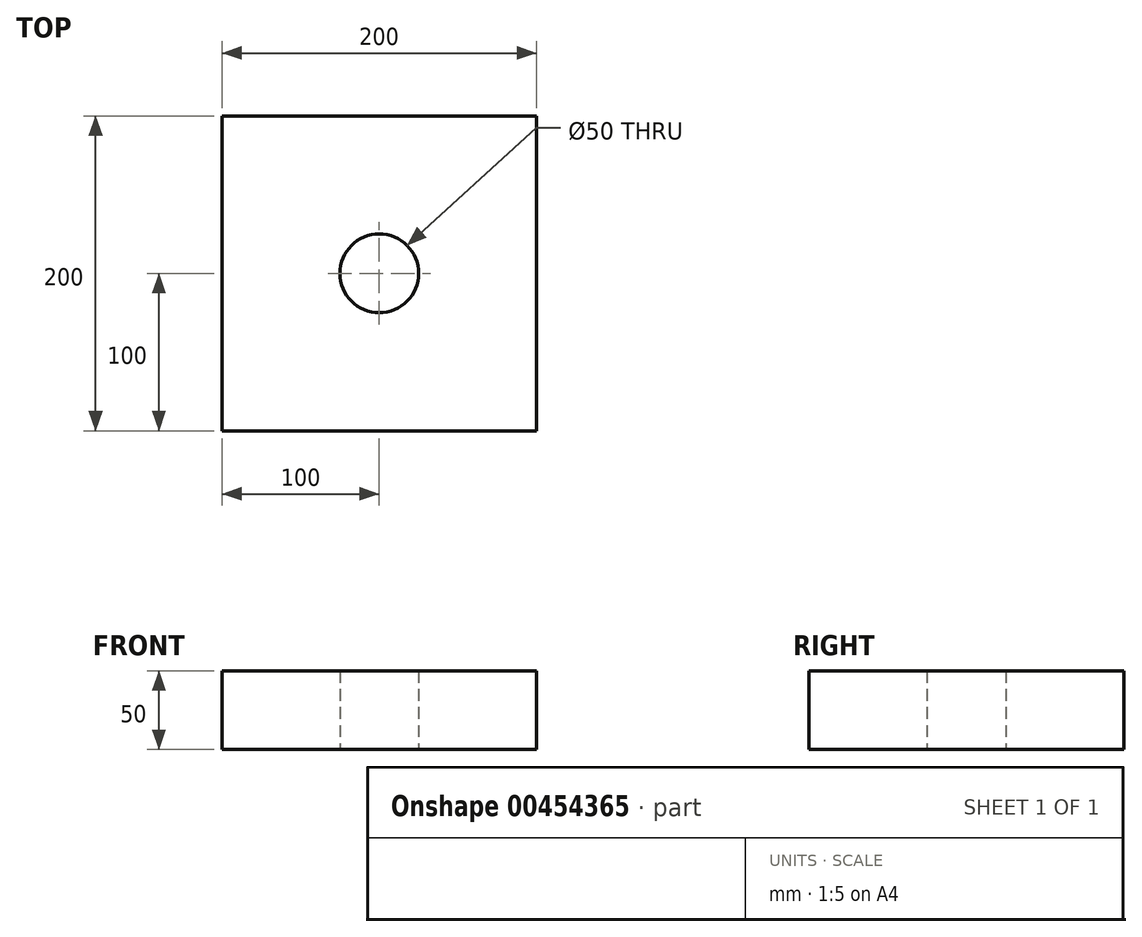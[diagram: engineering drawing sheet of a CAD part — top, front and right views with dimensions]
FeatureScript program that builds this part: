
annotation { "Feature Type Name" : "Feature", "Feature Type Description" : "" }
export const myFeature = defineFeature(function(context is Context, id is Id, definition is map)
    precondition{}
    {
        {
            var Q0;
            Q0=qCreatedBy(makeId("Top.planeOp"),FACE);
            var sketch = newSketch(context, id + "F0", { "sketchPlane" : qUnion([Q0])});
            skLineSegment(sketch, "E0.bottom", {"start": v(-100, -100) * mm, "end": v(100, -100) * mm});
            skLineSegment(sketch, "E0.top", {"start": v(-100, 100) * mm, "end": v(100, 100) * mm});
            skLineSegment(sketch, "E0.left", {"start": v(-100, -100) * mm, "end": v(-100, 100) * mm});
            skLineSegment(sketch, "E0.right", {"start": v(100, -100) * mm, "end": v(100, 100) * mm});
            skCircle(sketch, "E1", {"center": v(0, 0) * mm, "radius": 25 * mm});
            skSolve(sketch);
        }
        {
            var Q0;
            Q0=qSketchRegion(id+"F0",true);
            extrude(context, id + "F1", {"entities" : qUnion([Q0]), "depth" : 50 * mm});
        }
    });
